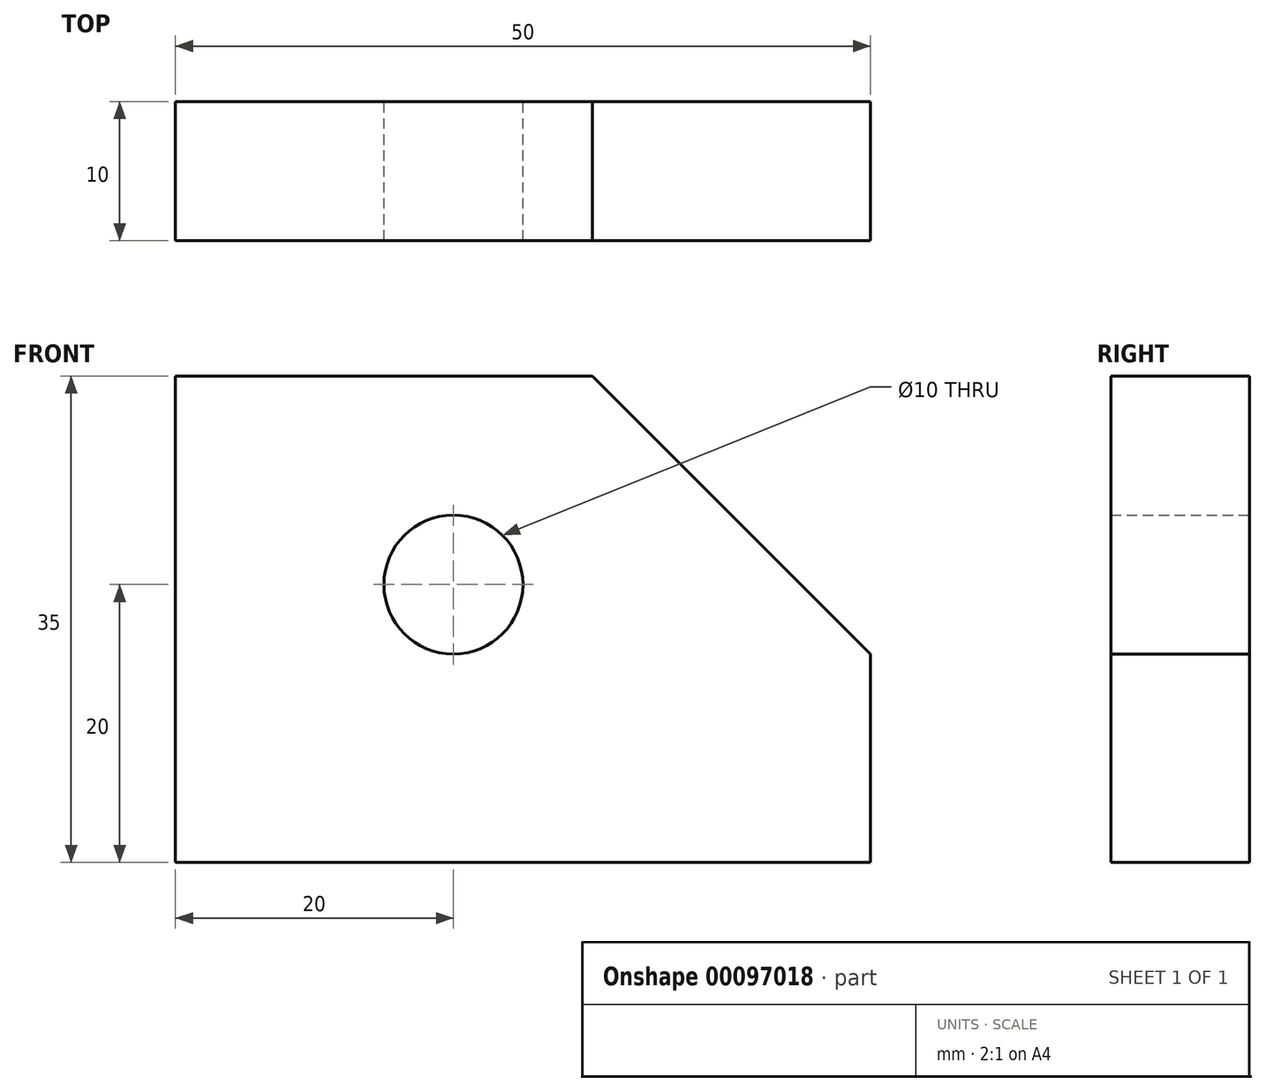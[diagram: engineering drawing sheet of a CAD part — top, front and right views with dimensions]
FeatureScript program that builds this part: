
annotation { "Feature Type Name" : "Feature", "Feature Type Description" : "" }
export const myFeature = defineFeature(function(context is Context, id is Id, definition is map)
    precondition{}
    {
        {
            var Q0;
            Q0=qCreatedBy(makeId("Front.planeOp"),FACE);
            var sketch = newSketch(context, id + "F0", { "sketchPlane" : qUnion([Q0])});
            skLineSegment(sketch, "E0", {"start": v(0, 0) * mm, "end": v(0, 35) * mm});
            skLineSegment(sketch, "E1", {"start": v(0, 35) * mm, "end": v(30, 35) * mm});
            skLineSegment(sketch, "E2", {"start": v(50, 15) * mm, "end": v(30, 35) * mm});
            skLineSegment(sketch, "E3", {"start": v(50, 15) * mm, "end": v(50, 0) * mm});
            skLineSegment(sketch, "E4", {"start": v(0, 0) * mm, "end": v(50, 0) * mm});
            skCircle(sketch, "E5", {"center": v(20, 20) * mm, "radius": 5 * mm});
            skSolve(sketch);
        }
        {
            var Q0;
            Q0=makeQuery(id+"F0.imprint","IMPRINT",FACE,{"disambiguationData":[TD([[makeQuery(id+"F0.imprint","IMPRINT",EDGE,{"derivedFrom":sQuery(id+"F0.wireOp",EDGE,"E0")}),-1.0]])]});
            extrude(context, id + "F1", {"entities" : qUnion([Q0]), "depth" : 10 * mm});
        }
    });
